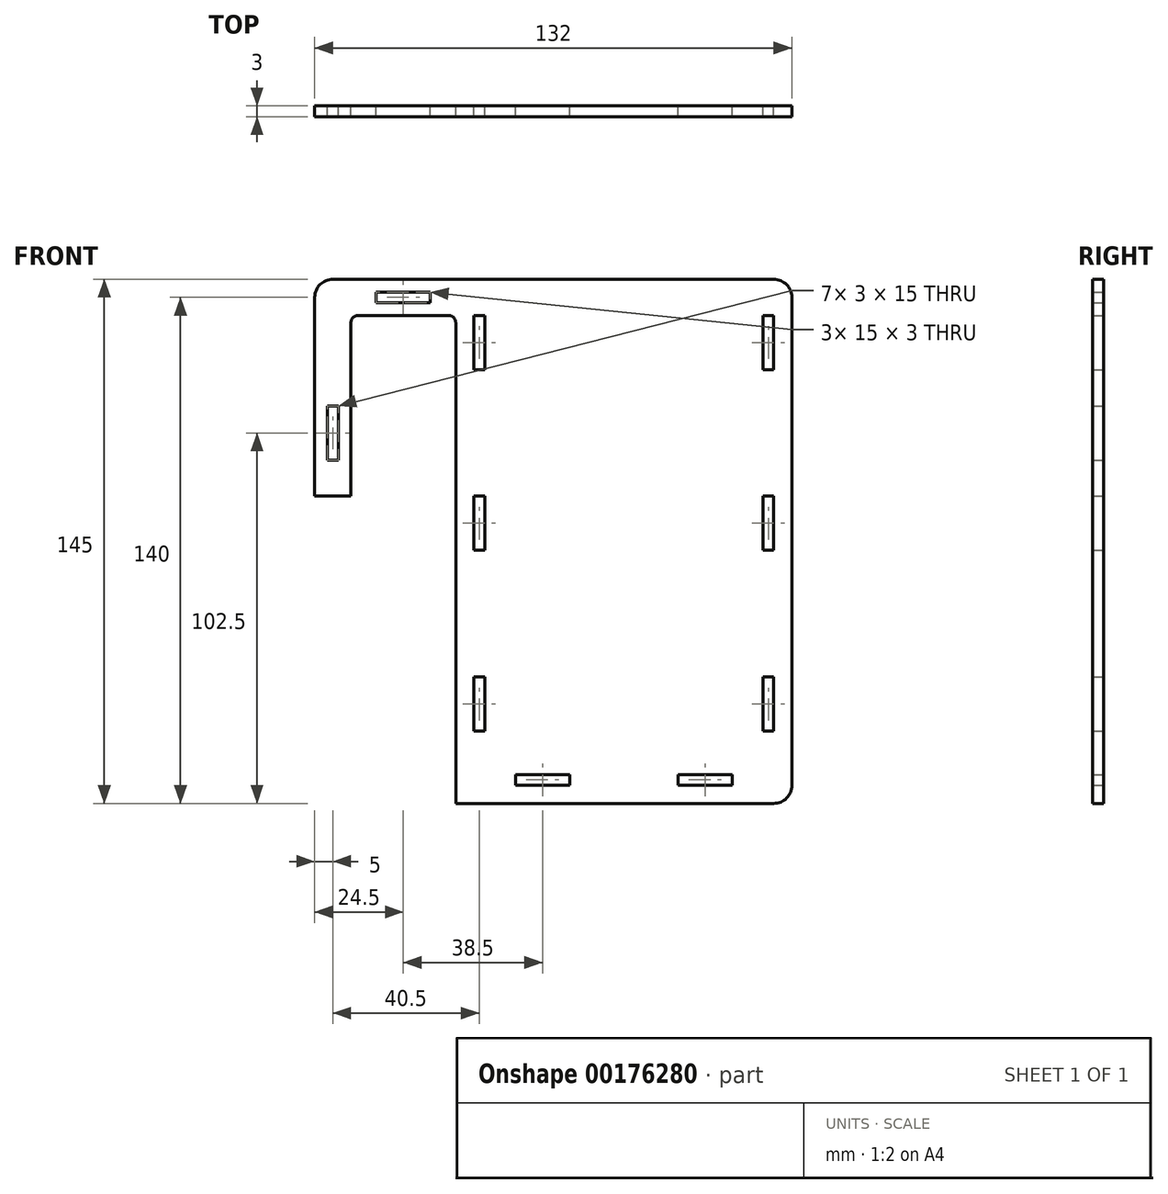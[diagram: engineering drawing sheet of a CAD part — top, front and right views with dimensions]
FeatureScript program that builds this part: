
annotation { "Feature Type Name" : "Feature", "Feature Type Description" : "" }
export const myFeature = defineFeature(function(context is Context, id is Id, definition is map)
    precondition{}
    {
        {
            assignVariable(context, id + "F0", {"name" : "e", "anyValue" : 3 * mm});
        }
        {
            var Q0;
            Q0=qCreatedBy(makeId("Front.planeOp"),FACE);
            var sketch = newSketch(context, id + "F1", { "sketchPlane" : qUnion([Q0])});
            skLineSegment(sketch, "E0", {"start": v(0, 0) * mm, "end": v(0, 55) * mm});
            skLineSegment(sketch, "E1", {"start": v(5, 60) * mm, "end": v(127, 60) * mm});
            skLineSegment(sketch, "E2", {"start": v(132, 55) * mm, "end": v(132, -80) * mm});
            skLineSegment(sketch, "E3", {"start": v(127, -85) * mm, "end": v(39, -85) * mm});
            skLineSegment(sketch, "E4", {"start": v(39, -85) * mm, "end": v(39, 48) * mm});
            skLineSegment(sketch, "E5", {"start": v(37, 50) * mm, "end": v(12, 50) * mm});
            skLineSegment(sketch, "E6", {"start": v(10, 48) * mm, "end": v(10, 0) * mm});
            skLineSegment(sketch, "E7", {"start": v(10, 0) * mm, "end": v(0, 0) * mm});
            skLineSegment(sketch, "E8.bottom", {"start": v(44, 50) * mm, "end": v(47, 50) * mm});
            skLineSegment(sketch, "E8.top", {"start": v(44, 35) * mm, "end": v(47, 35) * mm});
            skLineSegment(sketch, "E8.left", {"start": v(44, 50) * mm, "end": v(44, 35) * mm});
            skLineSegment(sketch, "E8.right", {"start": v(47, 50) * mm, "end": v(47, 35) * mm});
            skLineSegment(sketch, "E9.0.1.0", {"start": v(44, 0) * mm, "end": v(44, -15) * mm});
            skLineSegment(sketch, "E9.0.1.1", {"start": v(47, 0) * mm, "end": v(47, -15) * mm});
            skLineSegment(sketch, "E9.0.1.2", {"start": v(44, 0) * mm, "end": v(47, 0) * mm});
            skLineSegment(sketch, "E9.0.1.3", {"start": v(44, -15) * mm, "end": v(47, -15) * mm});
            skLineSegment(sketch, "E9.0.2.0", {"start": v(44, -50) * mm, "end": v(44, -65) * mm});
            skLineSegment(sketch, "E9.0.2.1", {"start": v(47, -50) * mm, "end": v(47, -65) * mm});
            skLineSegment(sketch, "E9.0.2.2", {"start": v(44, -50) * mm, "end": v(47, -50) * mm});
            skLineSegment(sketch, "E9.0.2.3", {"start": v(44, -65) * mm, "end": v(47, -65) * mm});
            skLineSegment(sketch, "E9.1.0.0", {"start": v(124, 50) * mm, "end": v(124, 35) * mm});
            skLineSegment(sketch, "E9.1.0.1", {"start": v(127, 50) * mm, "end": v(127, 35) * mm});
            skLineSegment(sketch, "E9.1.0.2", {"start": v(124, 50) * mm, "end": v(127, 50) * mm});
            skLineSegment(sketch, "E9.1.0.3", {"start": v(124, 35) * mm, "end": v(127, 35) * mm});
            skLineSegment(sketch, "E9.1.1.0", {"start": v(124, 0) * mm, "end": v(124, -15) * mm});
            skLineSegment(sketch, "E9.1.1.1", {"start": v(127, 0) * mm, "end": v(127, -15) * mm});
            skLineSegment(sketch, "E9.1.1.2", {"start": v(124, 0) * mm, "end": v(127, 0) * mm});
            skLineSegment(sketch, "E9.1.1.3", {"start": v(124, -15) * mm, "end": v(127, -15) * mm});
            skLineSegment(sketch, "E9.1.2.0", {"start": v(124, -50) * mm, "end": v(124, -65) * mm});
            skLineSegment(sketch, "E9.1.2.1", {"start": v(127, -50) * mm, "end": v(127, -65) * mm});
            skLineSegment(sketch, "E9.1.2.2", {"start": v(124, -50) * mm, "end": v(127, -50) * mm});
            skLineSegment(sketch, "E9.1.2.3", {"start": v(124, -65) * mm, "end": v(127, -65) * mm});
            skLineSegment(sketch, "E9.direction1", {"start": v(44, 35) * mm, "end": v(124, 35) * mm, "construction": true});
            skLineSegment(sketch, "E9.direction2", {"start": v(44, 35) * mm, "end": v(44, -15) * mm, "construction": true});
            skLineSegment(sketch, "E10.bottom", {"start": v(55.5, -77) * mm, "end": v(70.5, -77) * mm});
            skLineSegment(sketch, "E10.top", {"start": v(55.5, -80) * mm, "end": v(70.5, -80) * mm});
            skLineSegment(sketch, "E10.left", {"start": v(55.5, -77) * mm, "end": v(55.5, -80) * mm});
            skLineSegment(sketch, "E10.right", {"start": v(70.5, -77) * mm, "end": v(70.5, -80) * mm});
            skLineSegment(sketch, "E11", {"start": v(55.5, -80) * mm, "end": v(55.5, -85) * mm, "construction": true});
            skLineSegment(sketch, "E12", {"start": v(44, 35) * mm, "end": v(39, 35) * mm, "construction": true});
            skLineSegment(sketch, "E13", {"start": v(127, 35) * mm, "end": v(132, 35) * mm, "construction": true});
            skLineSegment(sketch, "E14", {"start": v(85.5, -85) * mm, "end": v(85.5, -64.8) * mm, "construction": true});
            skLineSegment(sketch, "E15.MirrorCS", {"start": v(115.5, -77) * mm, "end": v(115.5, -80) * mm});
            skLineSegment(sketch, "E16.MirrorCS", {"start": v(100.5, -77) * mm, "end": v(100.5, -80) * mm});
            skLineSegment(sketch, "E17.MirrorCS", {"start": v(115.5, -77) * mm, "end": v(100.5, -77) * mm});
            skLineSegment(sketch, "E18.MirrorCS", {"start": v(115.5, -80) * mm, "end": v(100.5, -80) * mm});
            skLineSegment(sketch, "E19.bottom", {"start": v(17, 56.5) * mm, "end": v(32, 56.5) * mm});
            skLineSegment(sketch, "E19.top", {"start": v(17, 53.5) * mm, "end": v(32, 53.5) * mm});
            skLineSegment(sketch, "E19.left", {"start": v(17, 56.5) * mm, "end": v(17, 53.5) * mm});
            skLineSegment(sketch, "E19.right", {"start": v(32, 56.5) * mm, "end": v(32, 53.5) * mm});
            skLineSegment(sketch, "E20.bottom", {"start": v(3.5, 25) * mm, "end": v(6.5, 25) * mm});
            skLineSegment(sketch, "E20.top", {"start": v(3.5, 10) * mm, "end": v(6.5, 10) * mm});
            skLineSegment(sketch, "E20.left", {"start": v(3.5, 25) * mm, "end": v(3.5, 10) * mm});
            skLineSegment(sketch, "E20.right", {"start": v(6.5, 25) * mm, "end": v(6.5, 10) * mm});
            skLineSegment(sketch, "E21", {"start": v(5, 10) * mm, "end": v(5, 0) * mm, "construction": true});
            skLineSegment(sketch, "E22", {"start": v(10, 50) * mm, "end": v(10, 60) * mm, "construction": true});
            skLineSegment(sketch, "E23", {"start": v(10, 55) * mm, "end": v(17, 55) * mm, "construction": true});
            skLineSegment(sketch, "E24", {"start": v(24.5, 53.5) * mm, "end": v(24.5, 50) * mm, "construction": true});
            skPoint(sketch, "E25.visualSharp", {"position": v(0, 60) * mm});
            skArc(sketch, "E25.filletArc", {"start": v(5, 60) * mm, "mid": v(1.46, 58.54) * mm, "end": v(0, 55) * mm});
            skPoint(sketch, "E26.visualSharp", {"position": v(10, 50) * mm});
            skArc(sketch, "E26.filletArc", {"start": v(12, 50) * mm, "mid": v(10.59, 49.41) * mm, "end": v(10, 48) * mm});
            skPoint(sketch, "E27.visualSharp", {"position": v(39, 50) * mm});
            skArc(sketch, "E27.filletArc", {"start": v(39, 48) * mm, "mid": v(38.41, 49.41) * mm, "end": v(37, 50) * mm});
            skPoint(sketch, "E28.visualSharp", {"position": v(132, 60) * mm});
            skArc(sketch, "E28.filletArc", {"start": v(132, 55) * mm, "mid": v(130.54, 58.54) * mm, "end": v(127, 60) * mm});
            skPoint(sketch, "E29.visualSharp", {"position": v(132, -85) * mm});
            skArc(sketch, "E29.filletArc", {"start": v(127, -85) * mm, "mid": v(130.54, -83.54) * mm, "end": v(132, -80) * mm});
            skSolve(sketch);
        }
        {
            var Q0;
            Q0 = qSketchRegion(id + "F1", true);
            extrude(context, id + "F2", {"entities" : qUnion([Q0]), "depth" : (getVariable(context, 'e'))});
        }
    });
